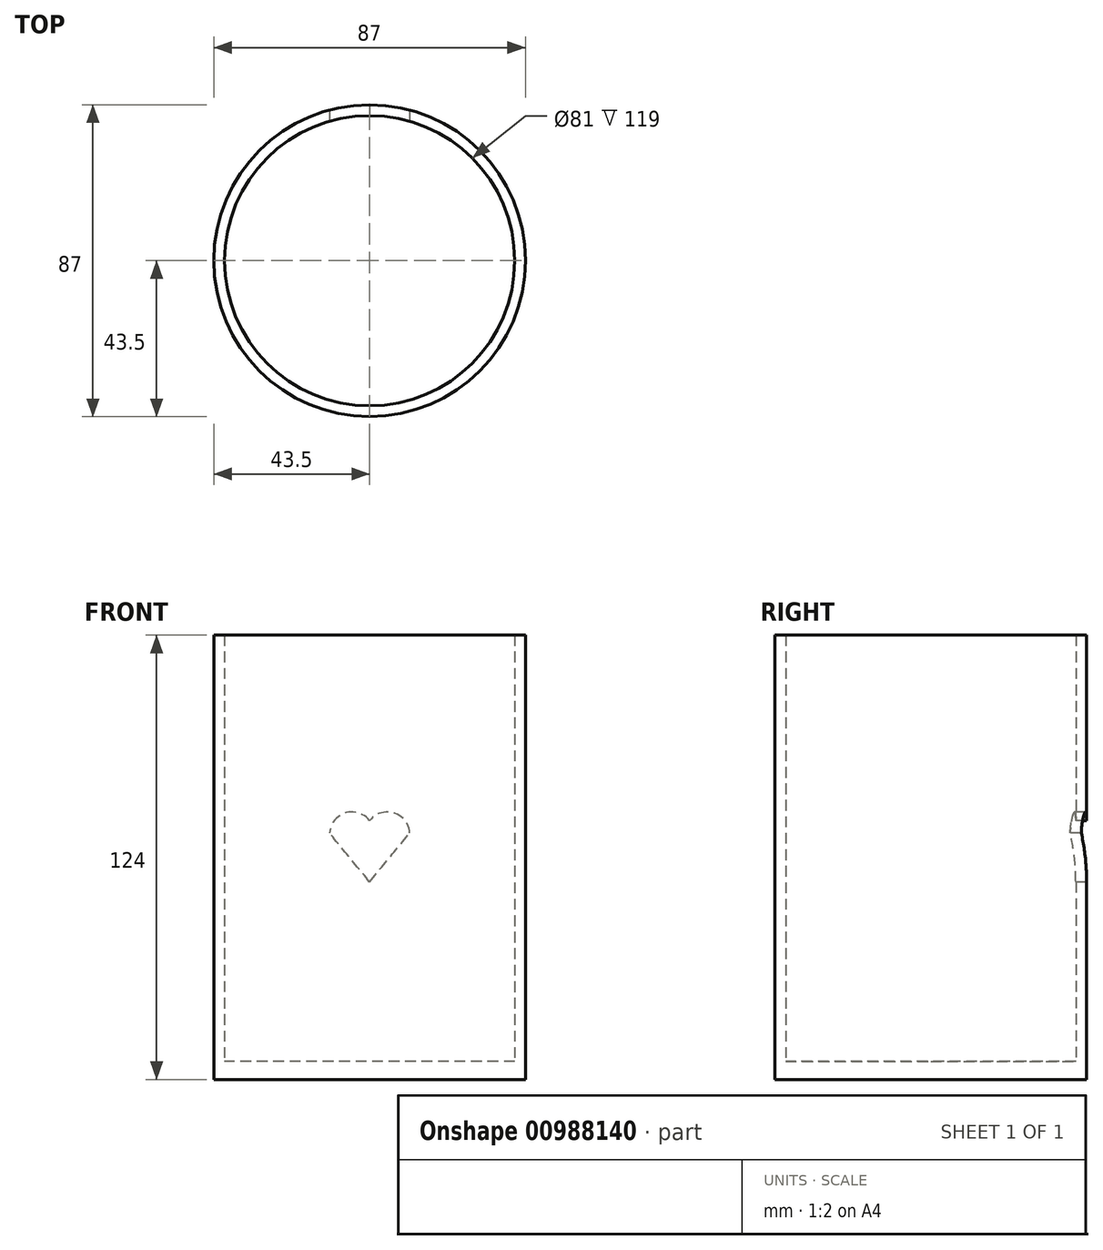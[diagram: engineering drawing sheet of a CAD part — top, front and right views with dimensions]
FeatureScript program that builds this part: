
annotation { "Feature Type Name" : "Feature", "Feature Type Description" : "" }
export const myFeature = defineFeature(function(context is Context, id is Id, definition is map)
    precondition{}
    {
        {
            var Q0;
            Q0=qCreatedBy(makeId("Top.planeOp"),FACE);
            var sketch = newSketch(context, id + "F0", { "sketchPlane" : qUnion([Q0])});
            skCircle(sketch, "E0", {"center": v(0, 0) * mm, "radius": 43.5 * mm});
            skCircle(sketch, "E1", {"center": v(0, 0) * mm, "radius": 40.5 * mm});
            skSolve(sketch);
        }
        {
            var Q0;
            Q0=makeQuery(id+"F0.imprint","IMPRINT",FACE,{"disambiguationData":[TD([[makeQuery(id+"F0.imprint","IMPRINT",EDGE,{"derivedFrom":sQuery(id+"F0.wireOp",EDGE,"E0")}),1.0]])]});
            extrude(context, id + "F1", {"entities" : qUnion([Q0]), "depth" : 124 * mm, "offsetDistance" : 25 * mm});
        }
        {
            var Q0;
            Q0=makeQuery(id+"F0.imprint","IMPRINT",FACE,{"disambiguationData":[TD([[makeQuery(id+"F0.imprint","IMPRINT",EDGE,{"derivedFrom":sQuery(id+"F0.wireOp",EDGE,"E1")}),1.0]])]});
            extrude(context, id + "F2", {"entities" : qUnion([Q0]), "operationType" : NewBodyOperationType.ADD, "depth" : 5 * mm, "offsetDistance" : 25 * mm});
        }
        {
            var Q0;
            Q0=qCreatedBy(makeId("Front.planeOp"),FACE);
            var sketch = newSketch(context, id + "F3", { "sketchPlane" : qUnion([Q0])});
            skLineSegment(sketch, "E2", {"start": v(0, 55.12) * mm, "end": v(-11.17, 68.76) * mm});
            skLineSegment(sketch, "E3", {"start": v(0, 55.12) * mm, "end": v(11.18, 68.75) * mm});
            skArc(sketch, "E4", {"start": v(0, 72.24) * mm, "mid": v(-6.8, 74.36) * mm, "end": v(-11.17, 68.76) * mm});
            skArc(sketch, "E5", {"start": v(11.18, 68.75) * mm, "mid": v(6.8, 74.37) * mm, "end": v(0, 72.24) * mm});
            skSolve(sketch);
        }
        {
            var Q0;
            Q0=makeQuery(id+"F3.imprint","IMPRINT",FACE,{"disambiguationData":[TD([[makeQuery(id+"F3.imprint","IMPRINT",EDGE,{"derivedFrom":sQuery(id+"F3.wireOp",EDGE,"E2")}),-1.0]])]});
            extrude(context, id + "F4", {"entities" : qUnion([Q0]), "operationType" : NewBodyOperationType.REMOVE, "endBound" : BoundingType.THROUGH_ALL, "oppositeDirection" : true, "depth" : 25 * mm, "offsetDistance" : 25 * mm});
        }
    });
